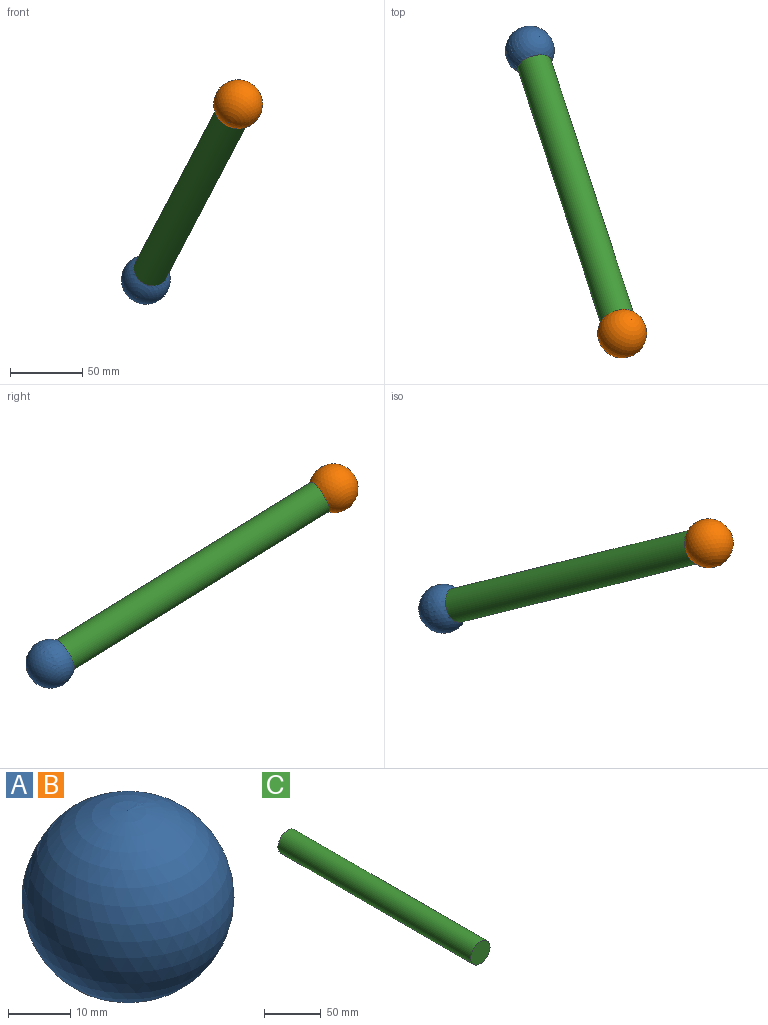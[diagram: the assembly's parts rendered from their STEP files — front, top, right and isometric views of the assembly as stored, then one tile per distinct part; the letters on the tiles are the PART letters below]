
ASSEMBLY  parts=3 mates=2
PART A: 3 faces, bbox 34x34x34 mm
  f0: sphere r=17mm, area 3102mm2, adj f1
  f1: cylinder r=12mm len=24mm, axis (0,-1,0), area 907.9mm2, adj f0,f2
  f2: plane 24x24mm, normal (0,1,0), area 452.4mm2, adj f1
PART B: same geometry as A
PART C: 3 faces, bbox 23.9x240x23.9 mm
  f0: cylinder r=11.95mm len=240mm, axis (0,1,0), area 18020.2mm2, adj f1,f2
  f1: plane 23.9x23.9mm, normal (0,-1,0), area 448.6mm2, adj f0
  f2: plane 23.9x23.9mm, normal (0,1,0), area 448.6mm2, adj f0
PLACE A rot(axis=(-0.23,-0.29,-0.93),171.7deg) t=(-225.64,-89.8,-77.5)mm
PLACE B rot(axis=(-0.77,0.61,0.19),44.4deg) t=(-161.54,-286.4,44.32)mm
PLACE C rot(axis=(0.07,-0.95,0.3),153.6deg) t=(-225.64,-89.8,-77.5)mm
MATE fastened B.f1 <-> C.f0  axis (-0.27,0.82,-0.51) through (-161.54,-286.4,44.32)mm
MATE fastened A.f1 <-> C.f0  axis (0.27,-0.82,0.51) through (-225.64,-89.8,-77.5)mm
